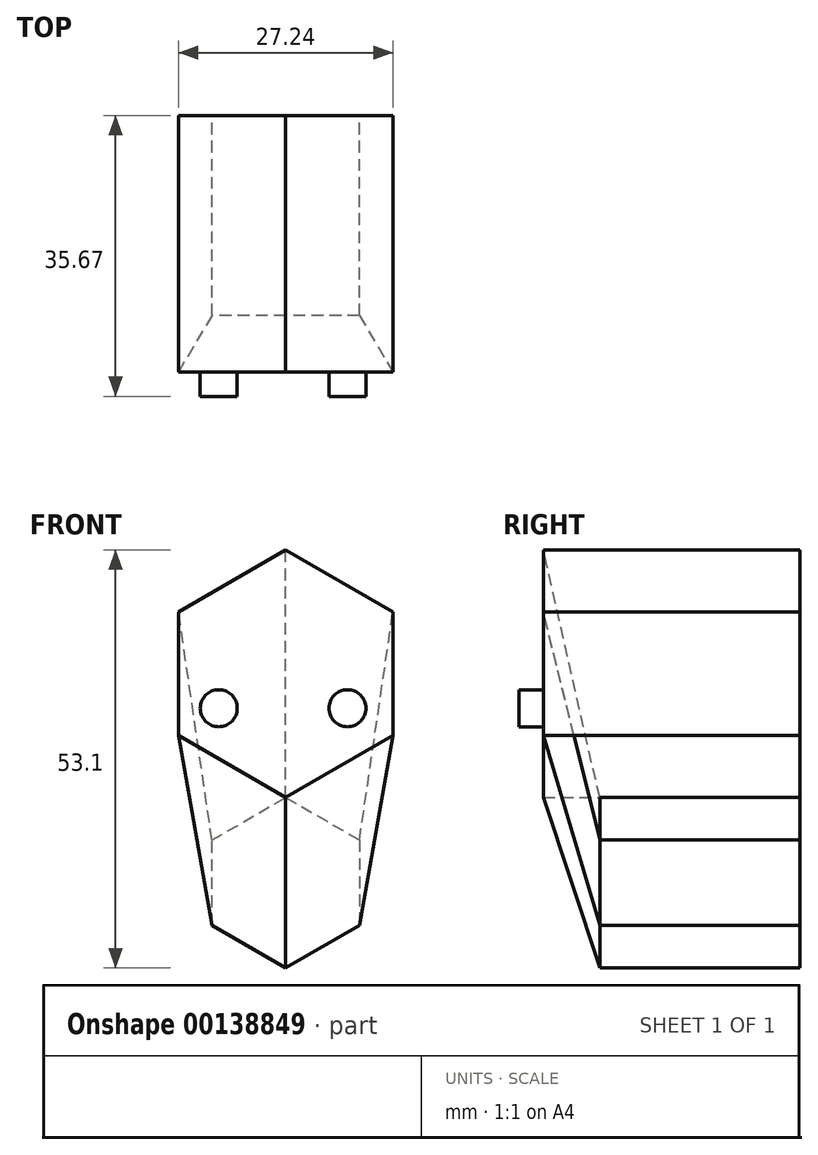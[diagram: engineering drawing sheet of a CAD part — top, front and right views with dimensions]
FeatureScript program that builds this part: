
annotation { "Feature Type Name" : "Feature", "Feature Type Description" : "" }
export const myFeature = defineFeature(function(context is Context, id is Id, definition is map)
    precondition{}
    {
        {
            var Q0;
            Q0=qCreatedBy(makeId("Front.planeOp"),FACE);
            var sketch = newSketch(context, id + "F0", { "sketchPlane" : qUnion([Q0])});
            skCircle(sketch, "E0.cCircle", {"center": v(0, 0) * mm, "radius": 9.37 * mm, "construction": true});
            skLineSegment(sketch, "E0.0", {"start": v(9.37, 5.4) * mm, "end": v(9.37, -5.4) * mm});
            skLineSegment(sketch, "E0.1", {"start": v(9.37, -5.4) * mm, "end": v(0, -10.82) * mm});
            skLineSegment(sketch, "E0.2", {"start": v(0, -10.82) * mm, "end": v(-9.37, -5.4) * mm});
            skLineSegment(sketch, "E0.3", {"start": v(-9.37, -5.4) * mm, "end": v(-9.37, 5.4) * mm});
            skLineSegment(sketch, "E0.4", {"start": v(-9.37, 5.4) * mm, "end": v(0, 10.82) * mm});
            skLineSegment(sketch, "E0.5", {"start": v(0, 10.82) * mm, "end": v(9.37, 5.4) * mm});
            skPoint(sketch, "E0.0.midPoint", {"position": v(9.37, 0) * mm});
            skCircle(sketch, "E1.cCircle", {"center": v(0, 26.55) * mm, "radius": 13.62 * mm, "construction": true});
            skLineSegment(sketch, "E1.0", {"start": v(13.62, 18.68) * mm, "end": v(0, 10.82) * mm});
            skLineSegment(sketch, "E1.1", {"start": v(0, 10.82) * mm, "end": v(-13.62, 18.68) * mm});
            skLineSegment(sketch, "E1.2", {"start": v(-13.62, 18.68) * mm, "end": v(-13.62, 34.42) * mm});
            skLineSegment(sketch, "E1.3", {"start": v(-13.62, 34.42) * mm, "end": v(0, 42.28) * mm});
            skLineSegment(sketch, "E1.4", {"start": v(0, 42.28) * mm, "end": v(13.62, 34.42) * mm});
            skLineSegment(sketch, "E1.5", {"start": v(13.62, 34.42) * mm, "end": v(13.62, 18.68) * mm});
            skPoint(sketch, "E1.0.midPoint", {"position": v(6.81, 14.75) * mm});
            skSolve(sketch);
        }
        {
            var Q0;
            Q0 = qSketchRegion(id + "F0", true);
            extrude(context, id + "F1", {"entities" : qUnion([Q0]), "depth" : 25.4 * mm});
        }
        {
            var Q0;
            Q0=makeQuery(id+"F1.opExtrude","CAP_FACE",FACE,{"disambiguationData":[OSD([sQuery(id+"F0.wireOp",EDGE,"E1.0"),sQuery(id+"F0.wireOp",EDGE,"E1.1"),sQuery(id+"F0.wireOp",EDGE,"E1.2"),sQuery(id+"F0.wireOp",EDGE,"E1.3"),sQuery(id+"F0.wireOp",EDGE,"E1.4"),sQuery(id+"F0.wireOp",EDGE,"E1.5")])],"isStart":false});
            var sketch = newSketch(context, id + "F2", { "sketchPlane" : qUnion([Q0])});
            skSolve(sketch);
        }
        {
            var Q0;
            Q0=makeQuery(id+"F2.imprint","IMPRINT",FACE,{"disambiguationData":[TD([[makeQuery(id+"F2.imprint","IMPRINT",EDGE,{"derivedFrom":makeQuery(id+"F1.opExtrude","CAP_EDGE",EDGE,{"disambiguationData":[OSD([sQuery(id+"F0.wireOp",EDGE,"E1.0")])],"isStart":false})}),-1.0]])]});
            extrude(context, id + "F3", {"entities" : qUnion([Q0]), "operationType" : NewBodyOperationType.ADD, "depth" : 7.16 * mm});
        }
        {
            var Q0;
            Q0=makeQuery(id+"F1.opExtrude","CAP_FACE",FACE,{"disambiguationData":[OSD([sQuery(id+"F0.wireOp",EDGE,"E0.0"),sQuery(id+"F0.wireOp",EDGE,"E0.1"),sQuery(id+"F0.wireOp",EDGE,"E0.2"),sQuery(id+"F0.wireOp",EDGE,"E0.3"),sQuery(id+"F0.wireOp",EDGE,"E0.4"),sQuery(id+"F0.wireOp",EDGE,"E0.5")])],"isStart":false});
            var Q1;
            Q1=makeQuery(id+"F3.opExtrude","CAP_FACE",FACE,{"disambiguationData":[OSD([sQuery(id+"F0.wireOp",EDGE,"E1.0"),sQuery(id+"F0.wireOp",EDGE,"E1.1"),sQuery(id+"F0.wireOp",EDGE,"E1.2"),sQuery(id+"F0.wireOp",EDGE,"E1.3"),sQuery(id+"F0.wireOp",EDGE,"E1.4"),sQuery(id+"F0.wireOp",EDGE,"E1.5")])],"isStart":false});
            loft(context, id + "F4", {"sheetProfilesArray" : [{ "sheetProfileEntities" : qUnion([Q0]) }, { "sheetProfileEntities" : qUnion([Q1]) }]});
        }
        {
            var Q0;
            Q0=makeQuery(id+"F3.opExtrude","CAP_FACE",FACE,{"disambiguationData":[OSD([sQuery(id+"F0.wireOp",EDGE,"E1.0"),sQuery(id+"F0.wireOp",EDGE,"E1.1"),sQuery(id+"F0.wireOp",EDGE,"E1.2"),sQuery(id+"F0.wireOp",EDGE,"E1.3"),sQuery(id+"F0.wireOp",EDGE,"E1.4"),sQuery(id+"F0.wireOp",EDGE,"E1.5")])],"isStart":false});
            var sketch = newSketch(context, id + "F5", { "sketchPlane" : qUnion([Q0])});
            skCircle(sketch, "E2", {"center": v(-8.5, 22.17) * mm, "radius": 2.35 * mm});
            skCircle(sketch, "E3", {"center": v(7.85, 22.17) * mm, "radius": 2.35 * mm});
            skSolve(sketch);
        }
        {
            var Q0;
            Q0=makeQuery(id+"F5.imprint","IMPRINT",FACE,{"disambiguationData":[TD([[makeQuery(id+"F5.imprint","IMPRINT",EDGE,{"derivedFrom":sQuery(id+"F5.wireOp",EDGE,"E2")}),1.0]])]});
            var Q1;
            Q1=makeQuery(id+"F5.imprint","IMPRINT",FACE,{"disambiguationData":[TD([[makeQuery(id+"F5.imprint","IMPRINT",EDGE,{"derivedFrom":sQuery(id+"F5.wireOp",EDGE,"E3")}),1.0]])]});
            extrude(context, id + "F6", {"entities" : qUnion([Q0, Q1]), "depth" : 3.1 * mm});
        }
    });
